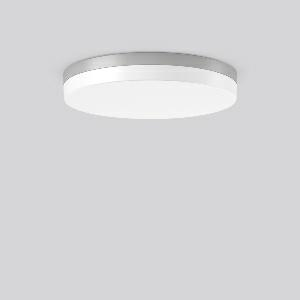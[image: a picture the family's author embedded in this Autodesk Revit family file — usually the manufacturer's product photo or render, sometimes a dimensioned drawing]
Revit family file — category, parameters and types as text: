
# Revit family: flat_slim_round_312634_004_730_377a
name_source: partatom
category: Lighting Fixtures
units: mm (PartAtom-declared; Revit-internal decimal feet)

## family parameters
Cut with Voids When Loaded = No
Host = Face
Light Source = No
Part Type = Normal
Room Calculation Point = No
Round Connector Dimension = Use Diameter
Shared = No

## types (1)
- MultiLumen 1 830 (1 x LED Modul 830, 3450 lm, 3000)
    Apparent Load = 26 VA
    CIE Flux Codes = 40 71 90 84 100
    Color Rendering = 80
    Color Temperature = 3000
    Default Elevation = 1800 mm
    Height = 70 mm
    Lamp = 1 x LED Modul 830
    Lamp Light Flux = 3450 lm
    Lamp count = 1
    Length = 480 mm
    Lifetime = 50000 h
    Luminous efficacy = 133 lm/W
    Manufacturer = RZB
    ModVariant = No
    Model = 312634.004.730
    Mounting Place = Ceiling
    Mounting Type = Surface mounted
    Number of Poles = 1
    OnlyDefault = Yes
    Power Factor = 1
    Product Name = FLAT SLIM round
    Product group = Surface mounted ceiling and wall luminaires
    ProductGroupID = 305
    Protection Class = Protection class I
    Protection Degree = Degree of protection
    RLX_Detail_Level = 1
    RLX_Emergency_Light_Flux = 0 lm
    RLX_Emergency_Type = 0
    RLX_Emergency_Type_DB = No
    RlxData = <blob elided: 21897 chars, md5=b095bf92>
    Socket = socket
    Standby Power = 0 W
    System Light Flux = 3450 lm
    System Power = 26 W
    Type Comments = MultiLumen 1 830
    Type Image = 312633.004.jpg
    URL = http://relux.com
    VarID = multilumen_1_830
    Voltage = 0 V
    Weight = 0.00 kg
    Width = 0 mm  [stored 0 ft]

note: [stored X ft] marks values corroborated as IEEE doubles in the binary element streams (Revit-internal decimal feet)

## geometry (parser evidence)
native form markers: Blend x4, Sweep x14
no freeform markers — native parametric forms only
